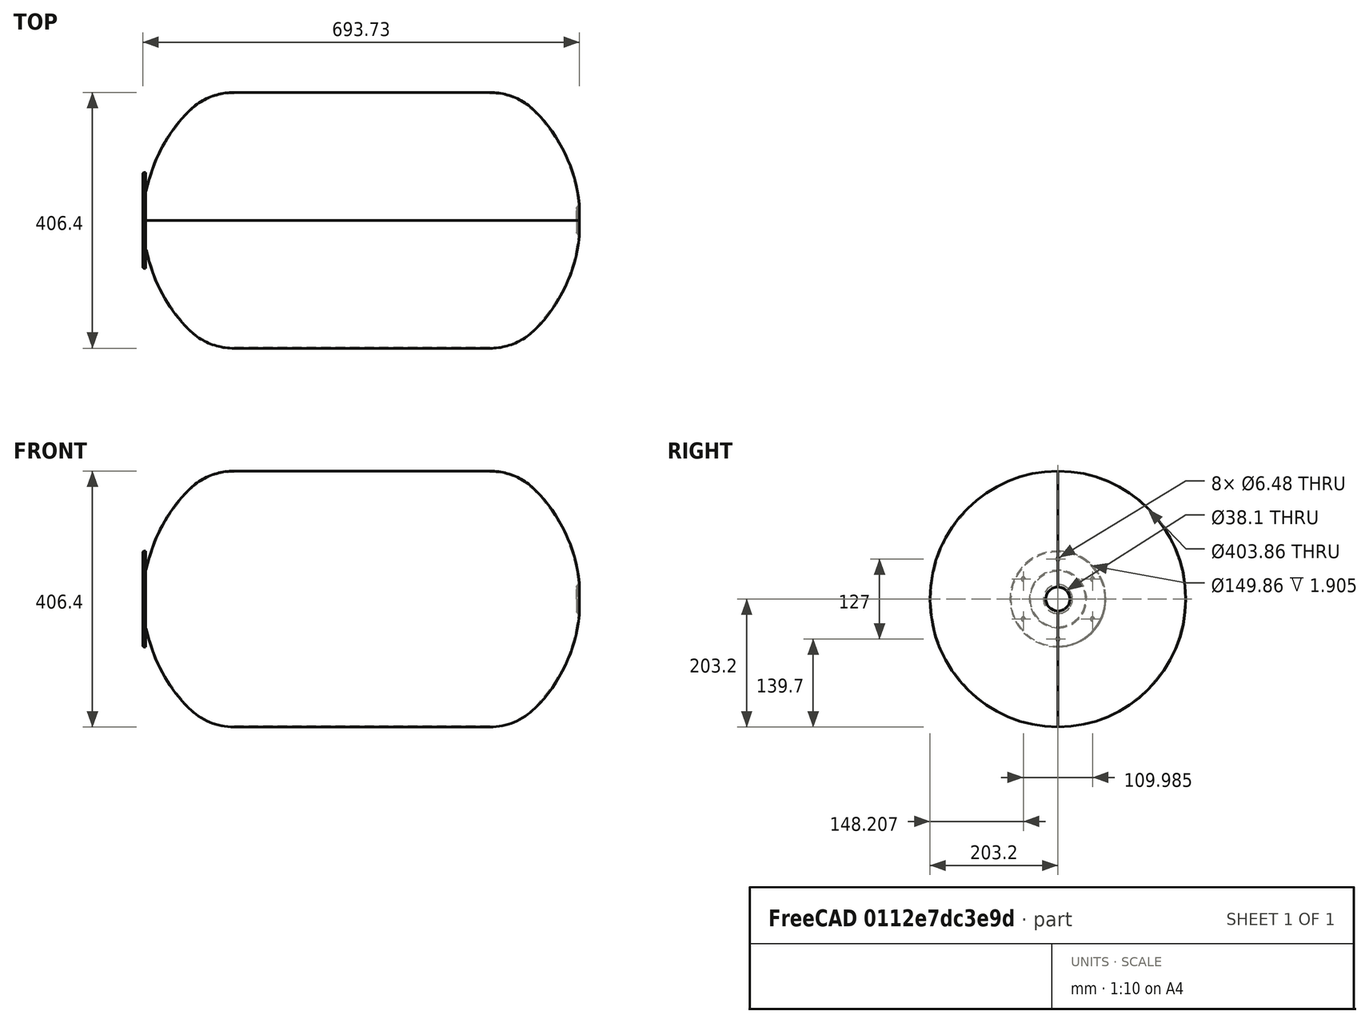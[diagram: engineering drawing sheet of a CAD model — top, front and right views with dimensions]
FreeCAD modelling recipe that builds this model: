
FCSTD DOCUMENT  (FreeCAD 0.20RUnknown)
Label: condencer-tank-section-y
License: All rights reserved
LicenseURL: http://en.wikipedia.org/wiki/All_rights_reserved
objects: Part::Feature×1, App::Link×1, Part::Compound×1, Part::Box×1, Part::Cut×1
note: 4 computed .brp shape members not serialized (recipe doc carries the construction recipe); baked Part::Feature solids carry a one-line shape summary decoded from their .brp

FEATURE [Part::Feature] Part__Feature  label="tank"
  shape: bbox 693.7 x 406.4 x 406.4 mm, 34 faces (baked)
FEATURE [App::Link] Part__Feature_CutLink
  LinkTransform = true
  LinkedObject = -> Part__Feature
FEATURE [Part::Compound] SectionCutCompound
  Links = -> [Part__Feature_CutLink]
FEATURE [Part::Box] SectionCutBoxY
  AttacherType = Attacher::AttachEngine3D
  Height = 407.4
  Length = 694.716
  Placement = pos=(-348.644,-407.4,-203.7) rot=(0,0,1;0rad)
  Width = 407.4
FEATURE [Part::Cut] SectionCutY  label="tank-section-y"
  Base = -> SectionCutCompound
  Tool = -> SectionCutBoxY
